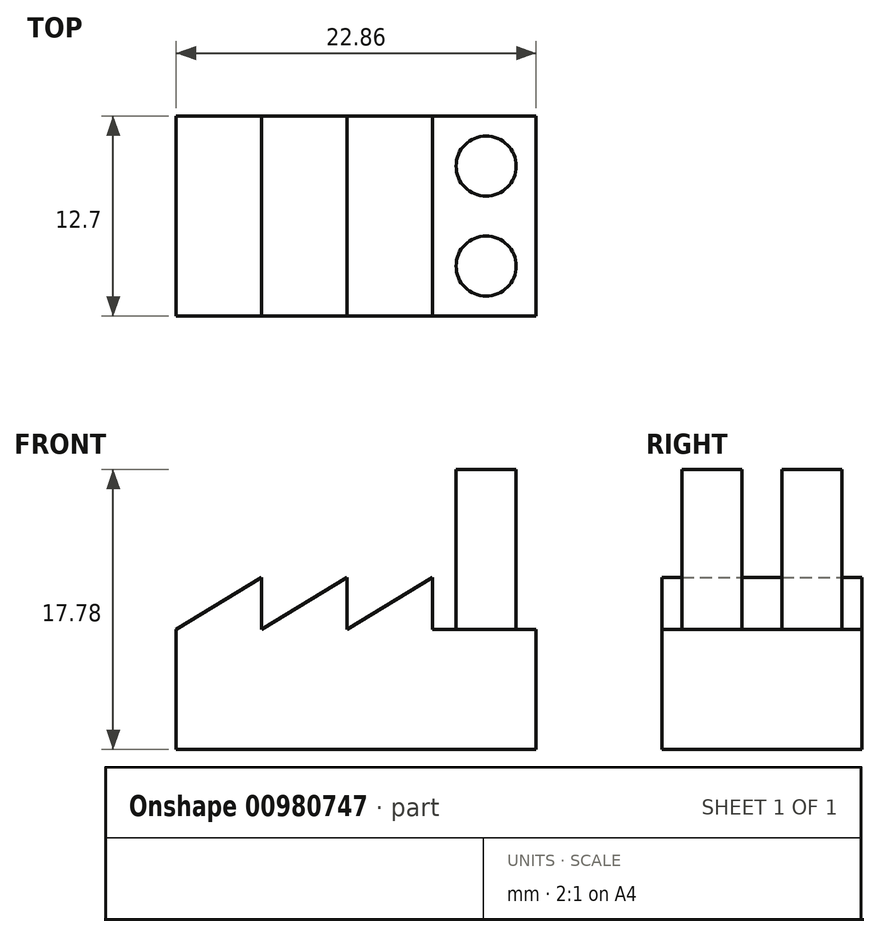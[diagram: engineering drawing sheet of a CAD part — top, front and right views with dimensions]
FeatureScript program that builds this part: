
annotation { "Feature Type Name" : "Feature", "Feature Type Description" : "" }
export const myFeature = defineFeature(function(context is Context, id is Id, definition is map)
    precondition{}
    {
        {
            var Q0;
            Q0=qCreatedBy(makeId("Front.planeOp"),FACE);
            var sketch = newSketch(context, id + "F0", { "sketchPlane" : qUnion([Q0])});
            skLineSegment(sketch, "E0.bottom", {"start": v(0, 1.23) * mm, "end": v(22.86, 1.23) * mm});
            skLineSegment(sketch, "E0.top", {"start": v(0, 8.85) * mm, "end": v(22.86, 8.85) * mm});
            skLineSegment(sketch, "E0.left", {"start": v(0, 1.23) * mm, "end": v(0, 8.85) * mm});
            skLineSegment(sketch, "E0.right", {"start": v(22.86, 1.23) * mm, "end": v(22.86, 8.85) * mm});
            skLineSegment(sketch, "E1", {"start": v(0, 8.85) * mm, "end": v(5.42, 12.16) * mm});
            skLineSegment(sketch, "E2", {"start": v(5.42, 12.16) * mm, "end": v(5.42, 8.85) * mm});
            skLineSegment(sketch, "E3", {"start": v(5.42, 8.85) * mm, "end": v(10.85, 12.16) * mm});
            skLineSegment(sketch, "E4", {"start": v(10.85, 12.16) * mm, "end": v(10.85, 8.85) * mm});
            skLineSegment(sketch, "E5", {"start": v(10.85, 8.85) * mm, "end": v(16.27, 12.16) * mm});
            skLineSegment(sketch, "E6", {"start": v(16.27, 12.16) * mm, "end": v(16.27, 8.85) * mm});
            skSolve(sketch);
        }
        {
            var Q0;
            Q0 = qSketchRegion(id + "F0", true);
            extrude(context, id + "F1", {"entities" : qUnion([Q0]), "depth" : 12.7 * mm, "offsetDistance" : 25.4 * mm});
        }
        {
            var Q0;
            Q0=makeQuery(id+"F1.opExtrude","SWEPT_FACE",FACE,{"disambiguationData":[OSD([sQuery(id+"F0.wireOp",EDGE,"E0.top")])]});
            var sketch = newSketch(context, id + "F2", { "sketchPlane" : qUnion([Q0])});
            skCircle(sketch, "E7", {"center": v(19.69, -3.18) * mm, "radius": 1.9 * mm});
            skCircle(sketch, "E8", {"center": v(19.69, -9.53) * mm, "radius": 1.9 * mm});
            skSolve(sketch);
        }
        {
            var Q0;
            Q0 = qSketchRegion(id + "F2", true);
            extrude(context, id + "F3", {"entities" : qUnion([Q0]), "operationType" : NewBodyOperationType.ADD, "depth" : 10.16 * mm, "offsetDistance" : 25.4 * mm});
        }
    });
